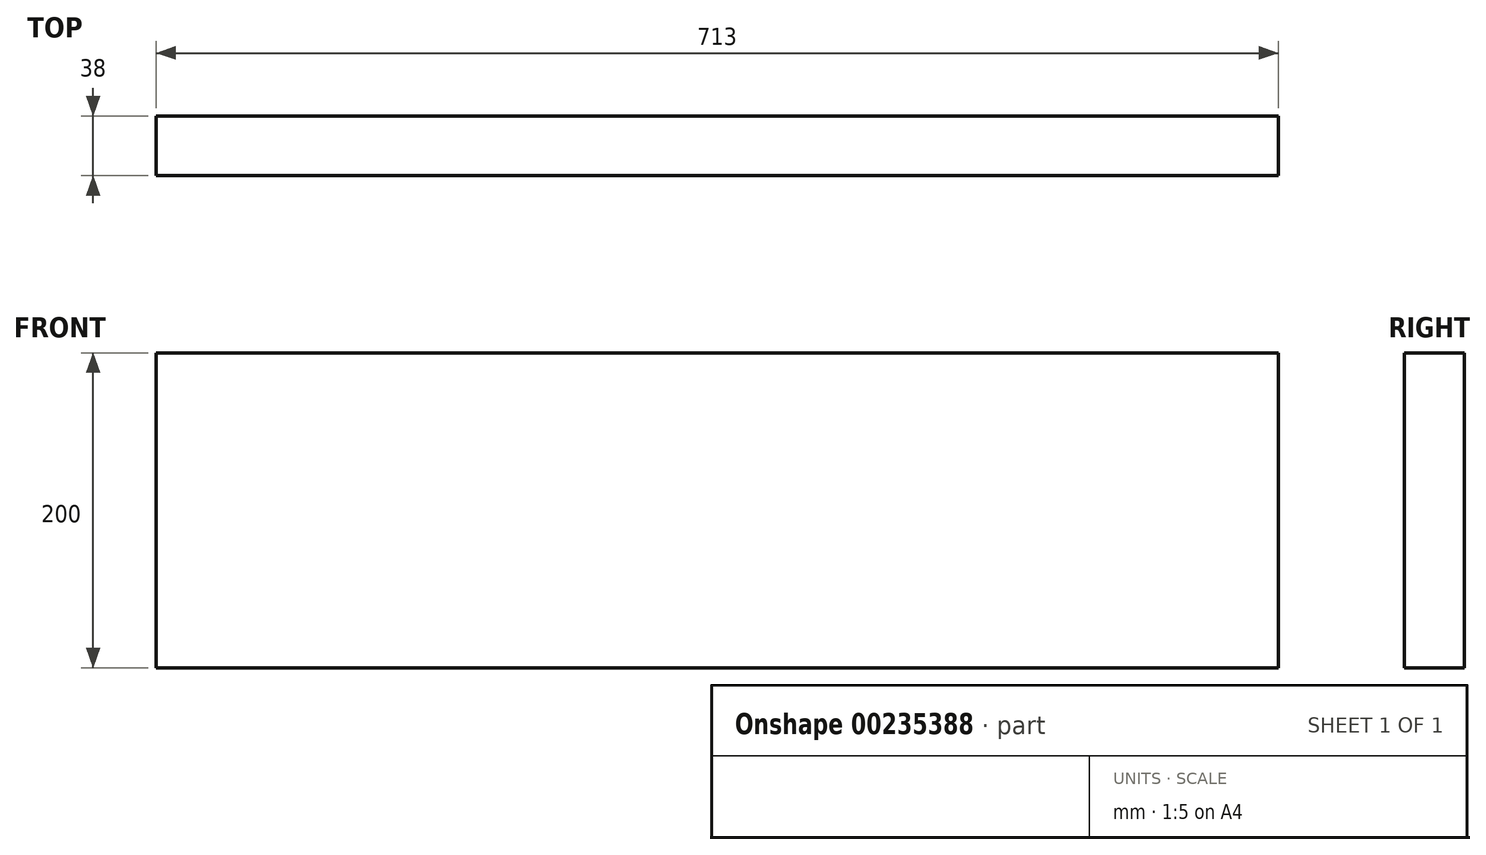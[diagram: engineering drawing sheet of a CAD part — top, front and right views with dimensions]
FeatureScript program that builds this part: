
annotation { "Feature Type Name" : "Feature", "Feature Type Description" : "" }
export const myFeature = defineFeature(function(context is Context, id is Id, definition is map)
    precondition{}
    {
        {
            var Q0;
            Q0=qCreatedBy(makeId("Front.planeOp"),FACE);
            var sketch = newSketch(context, id + "F0", { "sketchPlane" : qUnion([Q0])});
            skLineSegment(sketch, "E0.bottom", {"start": v(0, 0) * mm, "end": v(713, 0) * mm});
            skLineSegment(sketch, "E0.top", {"start": v(0, 200) * mm, "end": v(713, 200) * mm});
            skLineSegment(sketch, "E0.left", {"start": v(0, 0) * mm, "end": v(0, 200) * mm});
            skLineSegment(sketch, "E0.right", {"start": v(713, 0) * mm, "end": v(713, 200) * mm});
            skSolve(sketch);
        }
        {
            var Q0;
            Q0=makeQuery(id+"F0.imprint","IMPRINT",FACE,{"disambiguationData":[TD([[makeQuery(id+"F0.imprint","IMPRINT",EDGE,{"derivedFrom":sQuery(id+"F0.wireOp",EDGE,"E0.bottom")}),1.0]])]});
            extrude(context, id + "F1", {"entities" : qUnion([Q0]), "depth" : 38 * mm});
        }
    });
